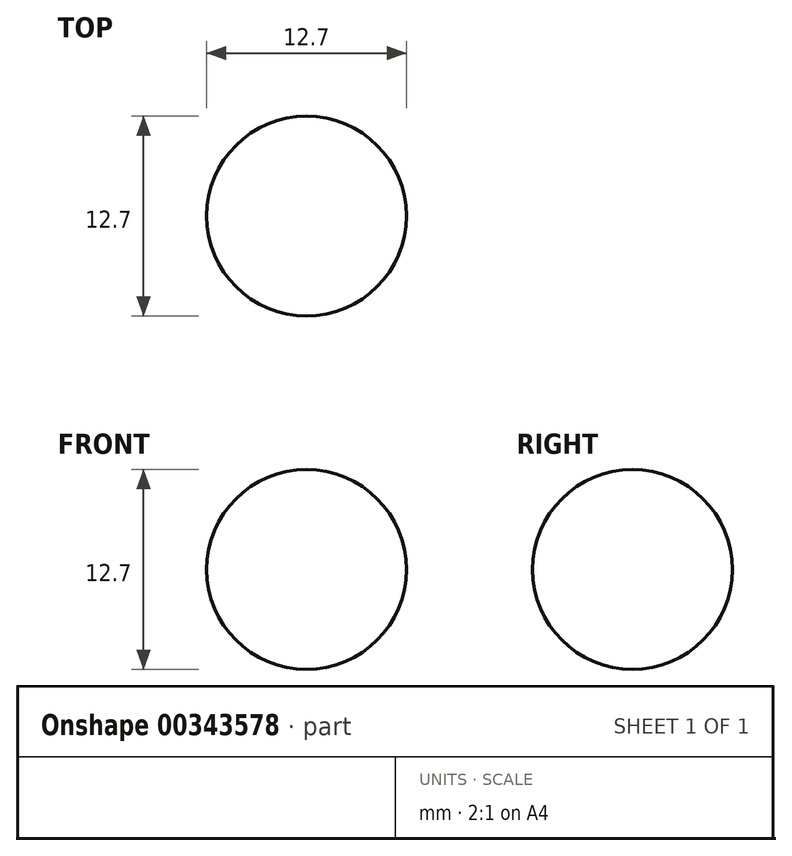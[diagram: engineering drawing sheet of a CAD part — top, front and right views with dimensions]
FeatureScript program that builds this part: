
annotation { "Feature Type Name" : "Feature", "Feature Type Description" : "" }
export const myFeature = defineFeature(function(context is Context, id is Id, definition is map)
    precondition{}
    {
        {
            var Q0;
            Q0=qCreatedBy(makeId("Top.planeOp"),FACE);
            var sketch = newSketch(context, id + "F0", { "sketchPlane" : qUnion([Q0])});
            skCircle(sketch, "E0", {"center": v(0, 0) * mm, "radius": 6.35 * mm});
            skSolve(sketch);
        }
        {
            var Q0;
            Q0 = qSketchRegion(id + "F0", true);
            extrude(context, id + "F1", {"entities" : qUnion([Q0]), "depth" : 12.7 * mm, "offsetDistance" : 25.4 * mm});
        }
        {
            var Q0;
            Q0=makeQuery(id+"F1.opExtrude","CAP_EDGE",EDGE,{"disambiguationData":[OSD([sQuery(id+"F0.wireOp",EDGE,"E0")])],"isStart":false});
            var Q1;
            Q1=makeQuery(id+"F1.opExtrude","CAP_EDGE",EDGE,{"disambiguationData":[OSD([sQuery(id+"F0.wireOp",EDGE,"E0")])],"isStart":true});
            fillet(context, id + "F2", {"entities" : qUnion([Q0, Q1]), "radius" : 6.35 * mm, "tangentPropagation" : true, "allowEdgeOverflow" : false});
        }
    });
